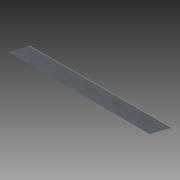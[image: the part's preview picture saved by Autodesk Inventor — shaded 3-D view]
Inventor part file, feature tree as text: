
AUTODESK INVENTOR PART (.ipt)
format: ipt  version: 2011 SP1 (Build 150282100, 282)  size: 70,144 bytes
history: native  units: in
note: dims shown in document units (in); Inventor stores cm internally (conversion verified against a paired STEP export)
features: extrude x1, sketch x1
ambient origin geometry x8: Origin, YZ Plane, XZ Plane, XY Plane, X Axis, Y Axis, Z Axis, Center Point
bodies: Solid1 (feature_tree)
feature tree (2):
  extrude  "Extrusion1"  Depth=26.1145in
  sketch  "Sketch1"  dims[d0=3.0in d1=26.1145in d2=4.0in d3=0.0625in d4=0.0in]
